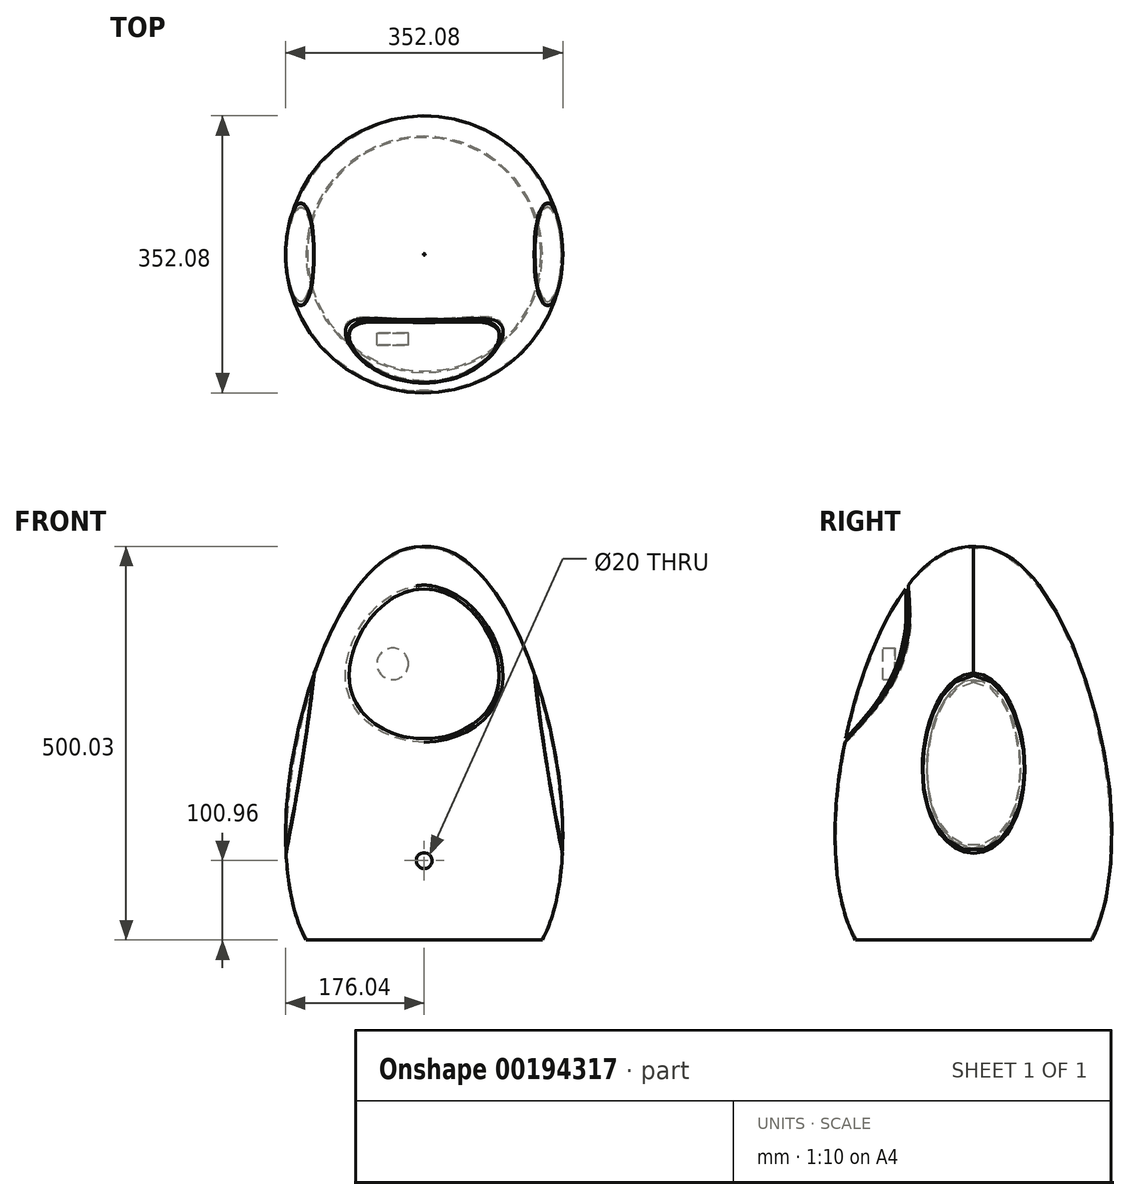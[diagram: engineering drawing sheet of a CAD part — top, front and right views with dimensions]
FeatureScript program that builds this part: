
annotation { "Feature Type Name" : "Feature", "Feature Type Description" : "" }
export const myFeature = defineFeature(function(context is Context, id is Id, definition is map)
    precondition{}
    {
        {
            var Q0;
            Q0=qCreatedBy(makeId("Front.planeOp"),FACE);
            var sketch = newSketch(context, id + "F0", { "sketchPlane" : qUnion([Q0])});
            skArc(sketch, "E0", {"start": v(0, -150) * mm, "mid": v(150, 0) * mm, "end": v(0, 150) * mm});
            skLineSegment(sketch, "E1", {"start": v(0, 150) * mm, "end": v(0, -150) * mm, "construction": true});
            skSolve(sketch);
        }
        {
            var Q0;
            Q0=sQuery(id+"F0.wireOp",EDGE,"E0");
            var Q1;
            Q1=sQuery(id+"F0.wireOp",EDGE,"E1");
            revolve(context, id + "F1", {"bodyType" : ToolBodyType.SURFACE, "surfaceEntities" : qUnion([Q0]), "axis" : qUnion([Q1]), "revolveType" : RevolveType.ONE_DIRECTION, "angle" : 360 * degree});
        }
        {
            var Q0;
            Q0=qCreatedBy(makeId("Front.planeOp"),FACE);
            var sketch = newSketch(context, id + "F2", { "sketchPlane" : qUnion([Q0])});
            skFitSpline(sketch, "E2", {"points": [v(1, 449.04) * mm, v(162.92, 203.43) * mm, v(150, -50.96) * mm], "startDerivative": vector(458.16, 11.78) * mm, "endDerivative": vector(-172.52, -317.15) * mm});
            skFitSpline(sketch, "E3.0", {"points": [v(1.05, 447.04) * mm, v(5.69, 447.16) * mm, v(14.81, 446.46) * mm, v(28.08, 442.76) * mm, v(40.93, 436.58) * mm, v(57.5, 425.25) * mm, v(77.03, 405.76) * mm, v(98.38, 375.34) * mm, v(117.4, 339.48) * mm, v(131.17, 306.37) * mm, v(140.86, 278.75) * mm, v(147.44, 257.65) * mm, v(153.31, 236.38) * mm, v(157.6, 218.67) * mm, v(160.66, 204.6) * mm, v(163.47, 190.65) * mm, v(166.52, 173.43) * mm, v(169.44, 153.16) * mm, v(172.38, 126.74) * mm, v(174.3, 94.99) * mm, v(173.94, 59.3) * mm, v(171.05, 26.48) * mm, v(165.76, -3.1) * mm, v(158.22, -28.98) * mm, v(151.78, -43.5) * mm, v(148.24, -50) * mm]});
            skLineSegment(sketch, "E4", {"start": v(1, 449.04) * mm, "end": v(1.05, 447.04) * mm});
            skLineSegment(sketch, "E5", {"start": v(148.24, -50) * mm, "end": v(150, -50.96) * mm});
            skLineSegment(sketch, "E6", {"start": v(0, 0) * mm, "end": v(0, 281.36) * mm, "construction": true});
            skSolve(sketch);
        }
        {
            var Q0;
            Q0=qCreatedBy(makeId("Front.planeOp"),FACE);
            cPlane(context, id + "F3", {"entities" : qUnion([Q0]), "cplaneType" : CPlaneType.OFFSET, "offset" : 100 * mm, "width" : 150 * mm, "height" : 150 * mm});
        }
        {
            var Q0;
            Q0=makeQuery(id+"F2.imprint","IMPRINT",FACE,{"disambiguationData":[TD([[makeQuery(id+"F2.imprint","IMPRINT",EDGE,{"derivedFrom":sQuery(id+"F2.wireOp",EDGE,"E2")}),-1.0]])]});
            var Q1;
            Q1=sQuery(id+"F2.wireOp",EDGE,"E6");
            revolve(context, id + "F4", {"entities" : qUnion([Q0]), "axis" : qUnion([Q1]), "revolveType" : RevolveType.ONE_DIRECTION, "oppositeDirection" : true, "angle" : 360 * degree});
        }
        {
            var Q0;
            Q0=qCreatedBy(makeId("Front.planeOp"),FACE);
            var sketch = newSketch(context, id + "F5", { "sketchPlane" : qUnion([Q0])});
            skLineSegment(sketch, "E7", {"start": v(0, 0) * mm, "end": v(0, 648.43) * mm, "construction": true});
            skFitSpline(sketch, "E8", {"points": [v(0, 400) * mm, v(-100, 280) * mm, v(0, 200) * mm], "startDerivative": vector(-337.34, -9.76) * mm, "endDerivative": vector(348.63, -14.37) * mm});
            skFitSpline(sketch, "E9.MirrorCS", {"points": [v(0, 400) * mm, v(100, 280) * mm, v(0, 200) * mm], "startDerivative": vector(337.34, -9.76) * mm, "endDerivative": vector(-348.63, -14.37) * mm});
            skFitSpline(sketch, "E10.0", {"points": [v(0.14, 395) * mm, v(-6.44, 394.81) * mm, v(-19.2, 392.68) * mm, v(-37.02, 384.96) * mm, v(-53.17, 373.42) * mm, v(-67.28, 358.83) * mm, v(-78.95, 342.01) * mm, v(-86.33, 326.86) * mm, v(-90.66, 314.5) * mm, v(-93.08, 305.23) * mm, v(-94.64, 296.06) * mm, v(-95.19, 288.6) * mm, v(-95.17, 282.81) * mm, v(-94.83, 277.15) * mm, v(-93.83, 270.3) * mm, v(-91.74, 262.48) * mm, v(-87.81, 252.57) * mm, v(-80.87, 241.2) * mm, v(-69.54, 229.36) * mm, v(-55.48, 219.53) * mm, v(-33.5, 209.41) * mm, v(-13.84, 205.57) * mm, v(0.2, 205) * mm]});
            skFitSpline(sketch, "E11.0", {"points": [v(-0.14, 395) * mm, v(6.44, 394.81) * mm, v(19.2, 392.68) * mm, v(37.02, 384.96) * mm, v(53.17, 373.42) * mm, v(67.28, 358.83) * mm, v(78.95, 342.01) * mm, v(86.33, 326.86) * mm, v(90.66, 314.5) * mm, v(93.08, 305.23) * mm, v(94.64, 296.06) * mm, v(95.19, 288.6) * mm, v(95.17, 282.81) * mm, v(94.83, 277.15) * mm, v(93.83, 270.3) * mm, v(91.74, 262.48) * mm, v(87.81, 252.57) * mm, v(80.87, 241.2) * mm, v(69.54, 229.36) * mm, v(55.48, 219.53) * mm, v(33.5, 209.41) * mm, v(13.84, 205.57) * mm, v(-0.2, 205) * mm]});
            skSolve(sketch);
        }
        {
            var Q0;
            Q0=qSketchRegion(id+"F5",true);
            extrude(context, id + "F6", {"entities" : qUnion([Q0]), "operationType" : NewBodyOperationType.REMOVE, "endBound" : BoundingType.THROUGH_ALL, "depth" : 25 * mm});
        }
        {
            var Q0;
            Q0=qCreatedBy(id+"F3.planeOp",FACE);
            var sketch = newSketch(context, id + "F7", { "sketchPlane" : qUnion([Q0])});
            skLineSegment(sketch, "E12", {"start": v(0, 214.33) * mm, "end": v(0, 353.6) * mm, "construction": true});
            skLineSegment(sketch, "E13", {"start": v(-40, 300) * mm, "end": v(41.8, 300) * mm, "construction": true});
            skCircle(sketch, "E14", {"center": v(-40, 300) * mm, "radius": 20 * mm});
            skCircle(sketch, "E15.MirrorC", {"center": v(40, 300) * mm, "radius": 20 * mm});
            skSolve(sketch);
        }
        {
            var Q0;
            Q0=makeQuery(id+"F7.imprint","IMPRINT",FACE,{"disambiguationData":[TD([[makeQuery(id+"F7.imprint","IMPRINT",EDGE,{"derivedFrom":sQuery(id+"F7.wireOp",EDGE,"E14")}),1.0]])]});
            var Q1;
            Q1=makeQuery(id+"F7.imprint","IMPRINT",FACE,{"disambiguationData":[TD([[makeQuery(id+"F7.imprint","IMPRINT",EDGE,{"derivedFrom":sQuery(id+"F7.wireOp",EDGE,"E15.MirrorC")}),-1.0]])]});
            extrude(context, id + "F8", {"entities" : qUnion([Q0, Q1]), "depth" : 15 * mm});
        }
        {
            var Q0;
            Q0=qCreatedBy(makeId("Front.planeOp"),FACE);
            var sketch = newSketch(context, id + "F9", { "sketchPlane" : qUnion([Q0])});
            skLineSegment(sketch, "E16", {"start": v(0, 0) * mm, "end": v(0, 181.26) * mm, "construction": true});
            skFitSpline(sketch, "E17", {"points": [v(136.25, 324.64) * mm, v(182.05, 26.05) * mm], "startDerivative": vector(13.21, -182.32) * mm, "endDerivative": vector(74.96, -372.11) * mm});
            skFitSpline(sketch, "E18.0", {"points": [v(137.24, 324.7) * mm, v(138.34, 309.54) * mm, v(142.04, 272.55) * mm, v(155.02, 177.4) * mm, v(170.54, 88.25) * mm, v(183.03, 26.25) * mm]});
            skLineSegment(sketch, "E19", {"start": v(136.25, 324.64) * mm, "end": v(137.24, 324.7) * mm});
            skLineSegment(sketch, "E20", {"start": v(182.05, 26.05) * mm, "end": v(183.03, 26.25) * mm});
            skFitSpline(sketch, "E21.MirrorCS", {"points": [v(-136.25, 324.64) * mm, v(-182.05, 26.05) * mm], "startDerivative": vector(-13.21, -182.32) * mm, "endDerivative": vector(-74.96, -372.11) * mm});
            skLineSegment(sketch, "E22.MirrorCS", {"start": v(-182.05, 26.05) * mm, "end": v(-183.03, 26.25) * mm});
            skLineSegment(sketch, "E23.MirrorCS", {"start": v(-136.25, 324.64) * mm, "end": v(-137.24, 324.7) * mm});
            skFitSpline(sketch, "E24.0", {"points": [v(-137.24, 324.7) * mm, v(-138.34, 309.54) * mm, v(-142.04, 272.55) * mm, v(-155.02, 177.4) * mm, v(-170.54, 88.25) * mm, v(-183.03, 26.25) * mm]});
            skSolve(sketch);
        }
        {
            var Q0;
            Q0=qSketchRegion(id+"F9",true);
            extrude(context, id + "F10", {"entities" : qUnion([Q0]), "operationType" : NewBodyOperationType.REMOVE, "endBound" : BoundingType.THROUGH_ALL, "oppositeDirection" : true, "depth" : 25 * mm, "hasSecondDirection" : true, "secondDirectionBound" : SecondDirectionBoundingType.THROUGH_ALL, "secondDirectionOppositeDirection" : false, "secondDirectionDepth" : 25 * mm});
        }
        {
            var Q0;
            Q0=qCreatedBy(makeId("Front.planeOp"),FACE);
            cPlane(context, id + "F11", {"entities" : qUnion([Q0]), "cplaneType" : CPlaneType.OFFSET, "offset" : 200 * mm, "width" : 150 * mm, "height" : 150 * mm});
        }
        {
            var Q0;
            Q0=qSketchRegion(id+"F9",true);
            extrude(context, id + "F12", {"entities" : qUnion([Q0]), "operationType" : NewBodyOperationType.REMOVE, "endBound" : BoundingType.THROUGH_ALL, "oppositeDirection" : true, "depth" : 25 * mm, "hasSecondDirection" : true, "secondDirectionBound" : SecondDirectionBoundingType.THROUGH_ALL, "secondDirectionOppositeDirection" : false, "secondDirectionDepth" : 25 * mm});
        }
        {
            var Q0;
            Q0=qCreatedBy(id+"F11.planeOp",FACE);
            var sketch = newSketch(context, id + "F13", { "sketchPlane" : qUnion([Q0])});
            skCircle(sketch, "E25", {"center": v(0, 50) * mm, "radius": 10 * mm});
            skSolve(sketch);
        }
        {
            var Q0;
            Q0=qSketchRegion(id+"F13",true);
            extrude(context, id + "F14", {"entities" : qUnion([Q0]), "operationType" : NewBodyOperationType.REMOVE, "oppositeDirection" : true, "depth" : 100 * mm});
        }
        {
            var Q0;
            Q0=qCreatedBy(makeId("Top.planeOp"),FACE);
            cPlane(context, id + "F15", {"entities" : qUnion([Q0]), "cplaneType" : CPlaneType.OFFSET, "offset" : 100 * mm, "oppositeDirection" : true, "width" : 150 * mm, "height" : 150 * mm});
        }
    });
